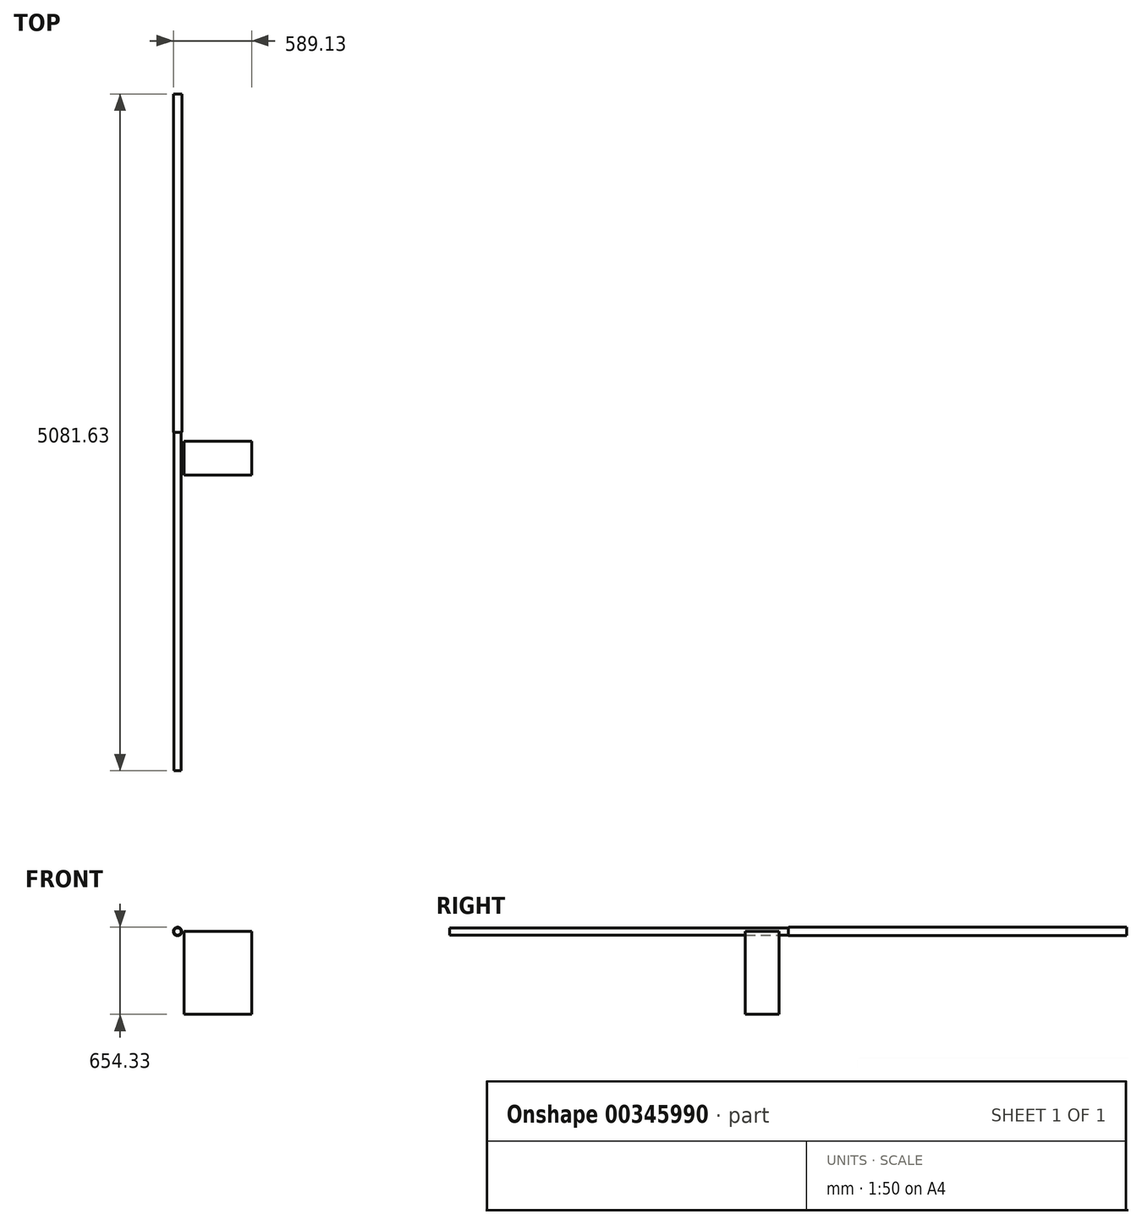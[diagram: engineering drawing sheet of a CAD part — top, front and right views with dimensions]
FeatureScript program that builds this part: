
annotation { "Feature Type Name" : "Feature", "Feature Type Description" : "" }
export const myFeature = defineFeature(function(context is Context, id is Id, definition is map)
    precondition{}
    {
        {
            var Q0;
            Q0=qCreatedBy(makeId("Front.planeOp"),FACE);
            var sketch = newSketch(context, id + "F0", { "sketchPlane" : qUnion([Q0])});
            skCircle(sketch, "E0", {"center": v(0, 0) * mm, "radius": 32.03 * mm});
            skSolve(sketch);
        }
        {
            var Q0;
            Q0 = qSketchRegion(id + "F0", true);
            extrude(context, id + "F1", {"entities" : qUnion([Q0]), "depth" : 2540 * mm});
        }
        {
            var Q0;
            Q0=makeQuery(id+"F1.opExtrude","CAP_EDGE",EDGE,{"disambiguationData":[OSD([sQuery(id+"F0.wireOp",EDGE,"E0")])],"isStart":false});
            fillet(context, id + "F2", {"entities" : qUnion([Q0]), "radius" : 5.08 * mm, "tangentPropagation" : true, "allowEdgeOverflow" : false});
        }
        {
            var Q0;
            Q0=makeQuery(id+"F1.opExtrude","CAP_FACE",FACE,{"disambiguationData":[OSD([sQuery(id+"F0.wireOp",EDGE,"E0")])],"isStart":false});
            extrude(context, id + "F3", {"entities" : qUnion([Q0]), "operationType" : NewBodyOperationType.ADD, "endBound" : BoundingType.THROUGH_ALL, "depth" : 25.4 * mm});
        }
        {
            var Q0;
            Q0=qCreatedBy(makeId("Top.planeOp"),FACE);
            var sketch = newSketch(context, id + "F4", { "sketchPlane" : qUnion([Q0])});
            skLineSegment(sketch, "E1.bottom", {"start": v(49.1, -2862.45) * mm, "end": v(557.1, -2862.45) * mm});
            skLineSegment(sketch, "E1.top", {"start": v(49.1, -2608.45) * mm, "end": v(557.1, -2608.45) * mm});
            skLineSegment(sketch, "E1.left", {"start": v(49.1, -2862.45) * mm, "end": v(49.1, -2608.45) * mm});
            skLineSegment(sketch, "E1.right", {"start": v(557.1, -2862.45) * mm, "end": v(557.1, -2608.45) * mm});
            skPoint(sketch, "E1.middle", {"position": v(303.1, -2735.45) * mm});
            skSolve(sketch);
        }
        {
            var Q0;
            Q0 = qSketchRegion(id + "F4", true);
            extrude(context, id + "F5", {"entities" : qUnion([Q0]), "oppositeDirection" : true, "depth" : 622.3 * mm});
        }
    });
